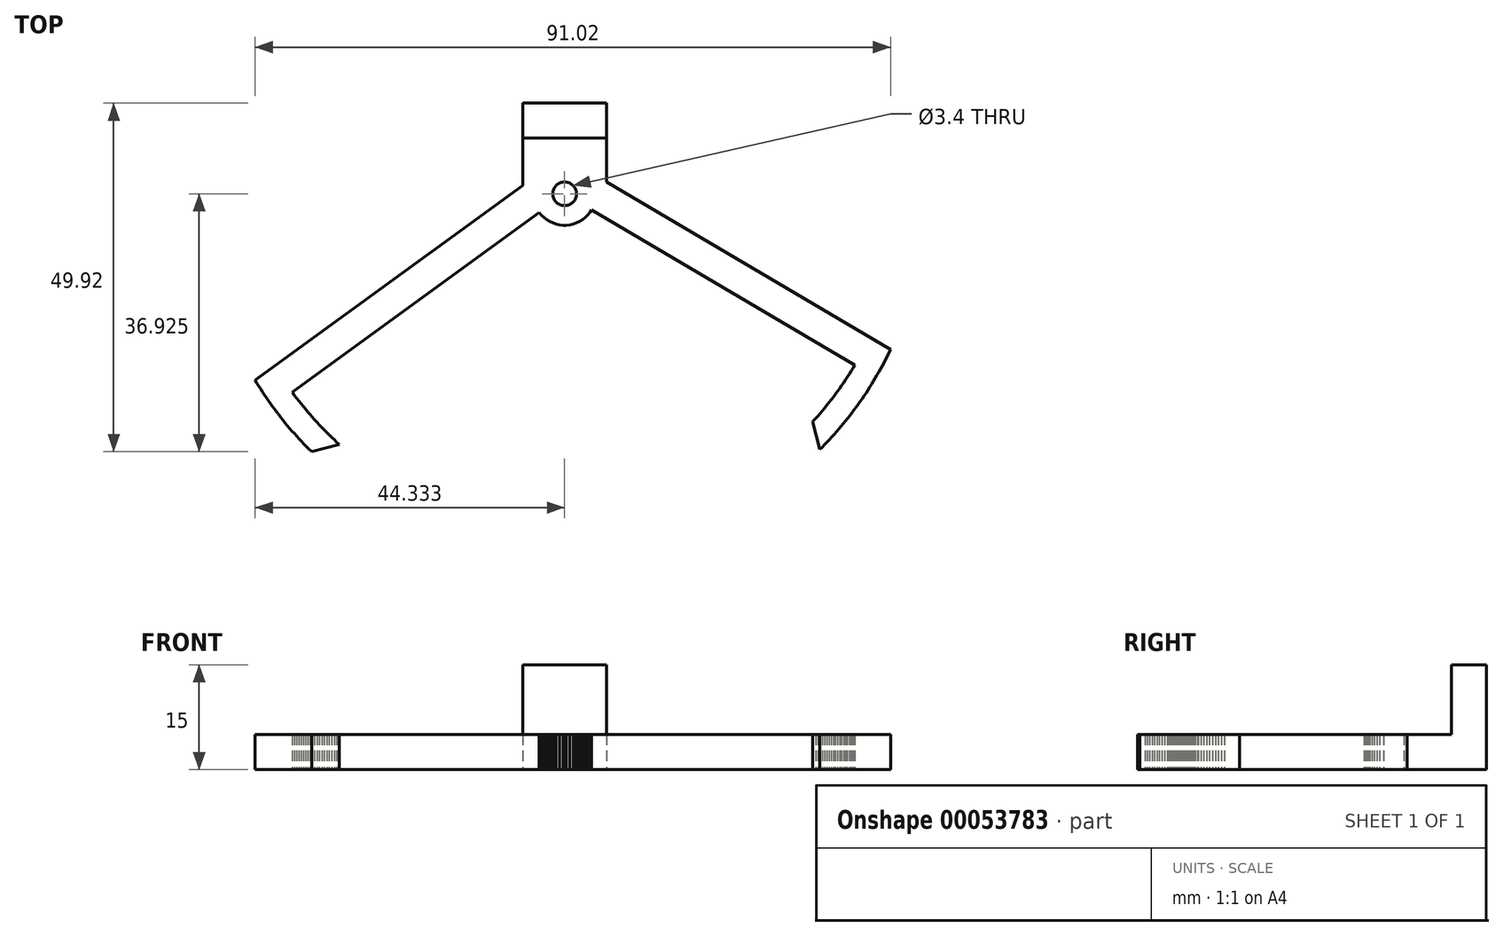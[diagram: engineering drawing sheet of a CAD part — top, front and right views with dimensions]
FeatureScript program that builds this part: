
annotation { "Feature Type Name" : "Feature", "Feature Type Description" : "" }
export const myFeature = defineFeature(function(context is Context, id is Id, definition is map)
    precondition{}
    {
        {
            var Q0;
            Q0=qCreatedBy(makeId("Top.planeOp"),FACE);
            var sketch = newSketch(context, id + "F0", { "sketchPlane" : qUnion([Q0])});
            skLineSegment(sketch, "E0", {"start": v(-33.44, -19.66) * mm, "end": v(-33.81, -19.33) * mm});
            skLineSegment(sketch, "E1", {"start": v(-33.81, -19.33) * mm, "end": v(-34.18, -18.99) * mm});
            skLineSegment(sketch, "E2", {"start": v(-34.18, -18.99) * mm, "end": v(-34.54, -18.64) * mm});
            skLineSegment(sketch, "E3", {"start": v(-34.54, -18.64) * mm, "end": v(-34.9, -18.3) * mm});
            skLineSegment(sketch, "E4", {"start": v(-34.9, -18.3) * mm, "end": v(-35.26, -17.95) * mm});
            skLineSegment(sketch, "E5", {"start": v(-35.26, -17.95) * mm, "end": v(-35.61, -17.6) * mm});
            skLineSegment(sketch, "E6", {"start": v(-35.61, -17.6) * mm, "end": v(-35.96, -17.23) * mm});
            skLineSegment(sketch, "E7", {"start": v(-35.96, -17.23) * mm, "end": v(-36.3, -16.87) * mm});
            skLineSegment(sketch, "E8", {"start": v(-36.3, -16.87) * mm, "end": v(-36.65, -16.5) * mm});
            skLineSegment(sketch, "E9", {"start": v(-36.65, -16.5) * mm, "end": v(-36.98, -16.13) * mm});
            skLineSegment(sketch, "E10", {"start": v(-36.98, -16.13) * mm, "end": v(-37.32, -15.76) * mm});
            skLineSegment(sketch, "E11", {"start": v(-37.32, -15.76) * mm, "end": v(-37.65, -15.39) * mm});
            skLineSegment(sketch, "E12", {"start": v(-37.65, -15.39) * mm, "end": v(-37.97, -15) * mm});
            skLineSegment(sketch, "E13", {"start": v(-37.97, -15) * mm, "end": v(-38.3, -14.62) * mm});
            skLineSegment(sketch, "E14", {"start": v(-38.3, -14.62) * mm, "end": v(-38.6, -14.24) * mm});
            skLineSegment(sketch, "E15", {"start": v(-38.6, -14.24) * mm, "end": v(-38.92, -13.85) * mm});
            skLineSegment(sketch, "E16", {"start": v(-38.92, -13.85) * mm, "end": v(-39.23, -13.45) * mm});
            skLineSegment(sketch, "E17", {"start": v(-39.23, -13.45) * mm, "end": v(-39.54, -13.06) * mm});
            skLineSegment(sketch, "E18", {"start": v(-39.54, -13.06) * mm, "end": v(-39.84, -12.66) * mm});
            skLineSegment(sketch, "E19", {"start": v(-39.84, -12.66) * mm, "end": v(-40.14, -12.26) * mm});
            skLineSegment(sketch, "E20", {"start": v(-40.14, -12.26) * mm, "end": v(-40.2, -12.17) * mm});
            skLineSegment(sketch, "E21", {"start": v(-40.2, -12.17) * mm, "end": v(-4.82, 13.57) * mm});
            skLineSegment(sketch, "E22", {"start": v(-4.82, 13.57) * mm, "end": v(-4.5, 13.18) * mm});
            skLineSegment(sketch, "E23", {"start": v(-4.5, 13.18) * mm, "end": v(-4.14, 12.83) * mm});
            skLineSegment(sketch, "E24", {"start": v(-4.14, 12.83) * mm, "end": v(-3.75, 12.52) * mm});
            skLineSegment(sketch, "E25", {"start": v(-3.75, 12.52) * mm, "end": v(-3.32, 12.26) * mm});
            skLineSegment(sketch, "E26", {"start": v(-3.32, 12.26) * mm, "end": v(-2.87, 12.05) * mm});
            skLineSegment(sketch, "E27", {"start": v(-2.87, 12.05) * mm, "end": v(-2.4, 11.88) * mm});
            skLineSegment(sketch, "E28", {"start": v(-2.4, 11.88) * mm, "end": v(-1.91, 11.78) * mm});
            skLineSegment(sketch, "E29", {"start": v(-1.91, 11.78) * mm, "end": v(-1.42, 11.72) * mm});
            skLineSegment(sketch, "E30", {"start": v(-1.42, 11.72) * mm, "end": v(-0.92, 11.72) * mm});
            skLineSegment(sketch, "E31", {"start": v(-0.92, 11.72) * mm, "end": v(-0.42, 11.78) * mm});
            skLineSegment(sketch, "E32", {"start": v(-0.42, 11.78) * mm, "end": v(0.07, 11.9) * mm});
            skLineSegment(sketch, "E33", {"start": v(0.07, 11.9) * mm, "end": v(0.54, 12.06) * mm});
            skLineSegment(sketch, "E34", {"start": v(0.54, 12.06) * mm, "end": v(1, 12.27) * mm});
            skLineSegment(sketch, "E35", {"start": v(1, 12.27) * mm, "end": v(1.41, 12.54) * mm});
            skLineSegment(sketch, "E36", {"start": v(1.41, 12.54) * mm, "end": v(1.8, 12.85) * mm});
            skLineSegment(sketch, "E37", {"start": v(1.8, 12.85) * mm, "end": v(2.16, 13.2) * mm});
            skLineSegment(sketch, "E38", {"start": v(2.16, 13.2) * mm, "end": v(2.48, 13.59) * mm});
            skLineSegment(sketch, "E39", {"start": v(2.48, 13.59) * mm, "end": v(2.7, 13.93) * mm});
            skLineSegment(sketch, "E40", {"start": v(2.7, 13.93) * mm, "end": v(40.39, -8.3) * mm});
            skLineSegment(sketch, "E41", {"start": v(40.39, -8.3) * mm, "end": v(40.13, -8.73) * mm});
            skLineSegment(sketch, "E42", {"start": v(40.13, -8.73) * mm, "end": v(39.87, -9.16) * mm});
            skLineSegment(sketch, "E43", {"start": v(39.87, -9.16) * mm, "end": v(39.6, -9.58) * mm});
            skLineSegment(sketch, "E44", {"start": v(39.6, -9.58) * mm, "end": v(39.34, -10) * mm});
            skLineSegment(sketch, "E45", {"start": v(39.34, -10) * mm, "end": v(39.06, -10.42) * mm});
            skLineSegment(sketch, "E46", {"start": v(39.06, -10.42) * mm, "end": v(38.78, -10.84) * mm});
            skLineSegment(sketch, "E47", {"start": v(38.78, -10.84) * mm, "end": v(38.5, -11.25) * mm});
            skLineSegment(sketch, "E48", {"start": v(38.5, -11.25) * mm, "end": v(38.21, -11.66) * mm});
            skLineSegment(sketch, "E49", {"start": v(38.21, -11.66) * mm, "end": v(37.92, -12.06) * mm});
            skLineSegment(sketch, "E50", {"start": v(37.92, -12.06) * mm, "end": v(37.63, -12.47) * mm});
            skLineSegment(sketch, "E51", {"start": v(37.63, -12.47) * mm, "end": v(37.33, -12.87) * mm});
            skLineSegment(sketch, "E52", {"start": v(37.33, -12.87) * mm, "end": v(37.03, -13.27) * mm});
            skLineSegment(sketch, "E53", {"start": v(37.03, -13.27) * mm, "end": v(36.72, -13.66) * mm});
            skLineSegment(sketch, "E54", {"start": v(36.72, -13.66) * mm, "end": v(36.4, -14.05) * mm});
            skLineSegment(sketch, "E55", {"start": v(36.4, -14.05) * mm, "end": v(36.1, -14.44) * mm});
            skLineSegment(sketch, "E56", {"start": v(36.1, -14.44) * mm, "end": v(35.77, -14.82) * mm});
            skLineSegment(sketch, "E57", {"start": v(35.77, -14.82) * mm, "end": v(35.45, -15.2) * mm});
            skLineSegment(sketch, "E58", {"start": v(35.45, -15.2) * mm, "end": v(35.12, -15.58) * mm});
            skLineSegment(sketch, "E59", {"start": v(35.12, -15.58) * mm, "end": v(34.79, -15.96) * mm});
            skLineSegment(sketch, "E60", {"start": v(34.79, -15.96) * mm, "end": v(34.45, -16.33) * mm});
            skLineSegment(sketch, "E61", {"start": v(34.45, -16.33) * mm, "end": v(34.38, -16.4) * mm});
            skLineSegment(sketch, "E62", {"start": v(34.38, -16.4) * mm, "end": v(35.4, -20.4) * mm});
            skLineSegment(sketch, "E63", {"start": v(35.4, -20.4) * mm, "end": v(35.74, -20.04) * mm});
            skLineSegment(sketch, "E64", {"start": v(35.74, -20.04) * mm, "end": v(36.1, -19.68) * mm});
            skLineSegment(sketch, "E65", {"start": v(36.1, -19.68) * mm, "end": v(36.44, -19.32) * mm});
            skLineSegment(sketch, "E66", {"start": v(36.44, -19.32) * mm, "end": v(36.78, -18.96) * mm});
            skLineSegment(sketch, "E67", {"start": v(36.78, -18.96) * mm, "end": v(37.12, -18.59) * mm});
            skLineSegment(sketch, "E68", {"start": v(37.12, -18.59) * mm, "end": v(37.45, -18.22) * mm});
            skLineSegment(sketch, "E69", {"start": v(37.45, -18.22) * mm, "end": v(37.78, -17.84) * mm});
            skLineSegment(sketch, "E70", {"start": v(37.78, -17.84) * mm, "end": v(38.1, -17.46) * mm});
            skLineSegment(sketch, "E71", {"start": v(38.1, -17.46) * mm, "end": v(38.43, -17.08) * mm});
            skLineSegment(sketch, "E72", {"start": v(38.43, -17.08) * mm, "end": v(38.75, -16.7) * mm});
            skLineSegment(sketch, "E73", {"start": v(38.75, -16.7) * mm, "end": v(39.07, -16.3) * mm});
            skLineSegment(sketch, "E74", {"start": v(39.07, -16.3) * mm, "end": v(39.38, -15.92) * mm});
            skLineSegment(sketch, "E75", {"start": v(39.38, -15.92) * mm, "end": v(39.69, -15.53) * mm});
            skLineSegment(sketch, "E76", {"start": v(39.69, -15.53) * mm, "end": v(40, -15.13) * mm});
            skLineSegment(sketch, "E77", {"start": v(40, -15.13) * mm, "end": v(40.3, -14.73) * mm});
            skLineSegment(sketch, "E78", {"start": v(40.3, -14.73) * mm, "end": v(40.6, -14.33) * mm});
            skLineSegment(sketch, "E79", {"start": v(40.6, -14.33) * mm, "end": v(40.89, -13.92) * mm});
            skLineSegment(sketch, "E80", {"start": v(40.89, -13.92) * mm, "end": v(41.17, -13.52) * mm});
            skLineSegment(sketch, "E81", {"start": v(41.17, -13.52) * mm, "end": v(41.46, -13.1) * mm});
            skLineSegment(sketch, "E82", {"start": v(41.46, -13.1) * mm, "end": v(41.74, -12.7) * mm});
            skLineSegment(sketch, "E83", {"start": v(41.74, -12.7) * mm, "end": v(42.02, -12.28) * mm});
            skLineSegment(sketch, "E84", {"start": v(42.02, -12.28) * mm, "end": v(42.3, -11.86) * mm});
            skLineSegment(sketch, "E85", {"start": v(42.3, -11.86) * mm, "end": v(42.56, -11.44) * mm});
            skLineSegment(sketch, "E86", {"start": v(42.56, -11.44) * mm, "end": v(42.83, -11.01) * mm});
            skLineSegment(sketch, "E87", {"start": v(42.83, -11.01) * mm, "end": v(43.09, -10.58) * mm});
            skLineSegment(sketch, "E88", {"start": v(43.09, -10.58) * mm, "end": v(43.34, -10.16) * mm});
            skLineSegment(sketch, "E89", {"start": v(43.34, -10.16) * mm, "end": v(43.6, -9.72) * mm});
            skLineSegment(sketch, "E90", {"start": v(43.6, -9.72) * mm, "end": v(43.85, -9.3) * mm});
            skLineSegment(sketch, "E91", {"start": v(43.85, -9.3) * mm, "end": v(44.09, -8.85) * mm});
            skLineSegment(sketch, "E92", {"start": v(44.09, -8.85) * mm, "end": v(44.33, -8.42) * mm});
            skLineSegment(sketch, "E93", {"start": v(44.33, -8.42) * mm, "end": v(44.57, -7.98) * mm});
            skLineSegment(sketch, "E94", {"start": v(44.57, -7.98) * mm, "end": v(44.8, -7.53) * mm});
            skLineSegment(sketch, "E95", {"start": v(44.8, -7.53) * mm, "end": v(45.02, -7.09) * mm});
            skLineSegment(sketch, "E96", {"start": v(45.02, -7.09) * mm, "end": v(45.25, -6.64) * mm});
            skLineSegment(sketch, "E97", {"start": v(45.25, -6.64) * mm, "end": v(45.47, -6.19) * mm});
            skLineSegment(sketch, "E98", {"start": v(45.47, -6.19) * mm, "end": v(45.51, -6.1) * mm});
            skLineSegment(sketch, "E99", {"start": v(45.51, -6.1) * mm, "end": v(1.1, 20.1) * mm});
            skLineSegment(sketch, "E100", {"start": v(1.1, 20.1) * mm, "end": v(0.67, 20.32) * mm});
            skLineSegment(sketch, "E101", {"start": v(0.67, 20.32) * mm, "end": v(0.2, 20.5) * mm});
            skLineSegment(sketch, "E102", {"start": v(0.2, 20.5) * mm, "end": v(-0.28, 20.63) * mm});
            skLineSegment(sketch, "E103", {"start": v(-0.28, 20.63) * mm, "end": v(-0.78, 20.7) * mm});
            skLineSegment(sketch, "E104", {"start": v(-0.78, 20.7) * mm, "end": v(-1.28, 20.71) * mm});
            skLineSegment(sketch, "E105", {"start": v(-1.28, 20.71) * mm, "end": v(-1.78, 20.67) * mm});
            skLineSegment(sketch, "E106", {"start": v(-1.78, 20.67) * mm, "end": v(-2.27, 20.58) * mm});
            skLineSegment(sketch, "E107", {"start": v(-2.27, 20.58) * mm, "end": v(-2.75, 20.43) * mm});
            skLineSegment(sketch, "E108", {"start": v(-2.75, 20.43) * mm, "end": v(-3.2, 20.23) * mm});
            skLineSegment(sketch, "E109", {"start": v(-3.2, 20.23) * mm, "end": v(-3.64, 19.98) * mm});
            skLineSegment(sketch, "E110", {"start": v(-3.64, 19.98) * mm, "end": v(-3.82, 19.85) * mm});
            skLineSegment(sketch, "E111", {"start": v(-3.82, 19.85) * mm, "end": v(-45.51, -10.47) * mm});
            skLineSegment(sketch, "E112", {"start": v(-45.51, -10.47) * mm, "end": v(-45.25, -10.9) * mm});
            skLineSegment(sketch, "E113", {"start": v(-45.25, -10.9) * mm, "end": v(-44.99, -11.32) * mm});
            skLineSegment(sketch, "E114", {"start": v(-44.99, -11.32) * mm, "end": v(-44.72, -11.74) * mm});
            skLineSegment(sketch, "E115", {"start": v(-44.72, -11.74) * mm, "end": v(-44.45, -12.16) * mm});
            skLineSegment(sketch, "E116", {"start": v(-44.45, -12.16) * mm, "end": v(-44.17, -12.58) * mm});
            skLineSegment(sketch, "E117", {"start": v(-44.17, -12.58) * mm, "end": v(-43.89, -13) * mm});
            skLineSegment(sketch, "E118", {"start": v(-43.89, -13) * mm, "end": v(-43.6, -13.4) * mm});
            skLineSegment(sketch, "E119", {"start": v(-43.6, -13.4) * mm, "end": v(-43.32, -13.81) * mm});
            skLineSegment(sketch, "E120", {"start": v(-43.32, -13.81) * mm, "end": v(-43.02, -14.22) * mm});
            skLineSegment(sketch, "E121", {"start": v(-43.02, -14.22) * mm, "end": v(-42.73, -14.62) * mm});
            skLineSegment(sketch, "E122", {"start": v(-42.73, -14.62) * mm, "end": v(-42.43, -15.02) * mm});
            skLineSegment(sketch, "E123", {"start": v(-42.43, -15.02) * mm, "end": v(-42.13, -15.42) * mm});
            skLineSegment(sketch, "E124", {"start": v(-42.13, -15.42) * mm, "end": v(-41.82, -15.81) * mm});
            skLineSegment(sketch, "E125", {"start": v(-41.82, -15.81) * mm, "end": v(-41.5, -16.2) * mm});
            skLineSegment(sketch, "E126", {"start": v(-41.5, -16.2) * mm, "end": v(-41.2, -16.6) * mm});
            skLineSegment(sketch, "E127", {"start": v(-41.2, -16.6) * mm, "end": v(-40.87, -16.98) * mm});
            skLineSegment(sketch, "E128", {"start": v(-40.87, -16.98) * mm, "end": v(-40.55, -17.36) * mm});
            skLineSegment(sketch, "E129", {"start": v(-40.55, -17.36) * mm, "end": v(-40.22, -17.74) * mm});
            skLineSegment(sketch, "E130", {"start": v(-40.22, -17.74) * mm, "end": v(-39.9, -18.12) * mm});
            skLineSegment(sketch, "E131", {"start": v(-39.9, -18.12) * mm, "end": v(-39.56, -18.49) * mm});
            skLineSegment(sketch, "E132", {"start": v(-39.56, -18.49) * mm, "end": v(-39.22, -18.86) * mm});
            skLineSegment(sketch, "E133", {"start": v(-39.22, -18.86) * mm, "end": v(-38.88, -19.22) * mm});
            skLineSegment(sketch, "E134", {"start": v(-38.88, -19.22) * mm, "end": v(-38.54, -19.59) * mm});
            skLineSegment(sketch, "E135", {"start": v(-38.54, -19.59) * mm, "end": v(-38.2, -19.95) * mm});
            skLineSegment(sketch, "E136", {"start": v(-38.2, -19.95) * mm, "end": v(-37.84, -20.3) * mm});
            skLineSegment(sketch, "E137", {"start": v(-37.84, -20.3) * mm, "end": v(-37.48, -20.65) * mm});
            skLineSegment(sketch, "E138", {"start": v(-37.48, -20.65) * mm, "end": v(-37.42, -20.71) * mm});
            skLineSegment(sketch, "E139", {"start": v(-37.42, -20.71) * mm, "end": v(-33.44, -19.66) * mm});
            skCircle(sketch, "E140", {"center": v(-1.18, 16.21) * mm, "radius": 1.7 * mm});
            skPoint(sketch, "E141", {"position": v(-7.24, 17.37) * mm});
            skLineSegment(sketch, "E142", {"start": v(-2.68, 29.21) * mm, "end": v(-2.68, 24.21) * mm});
            skLineSegment(sketch, "E143", {"start": v(0.32, 29.21) * mm, "end": v(0.32, 24.21) * mm});
            skLineSegment(sketch, "E144", {"start": v(-7.18, 29.21) * mm, "end": v(4.82, 29.21) * mm});
            skLineSegment(sketch, "E145", {"start": v(-7.18, 24.21) * mm, "end": v(4.82, 24.21) * mm});
            skLineSegment(sketch, "E146", {"start": v(4.82, 13.73) * mm, "end": v(4.82, 29.21) * mm});
            skLineSegment(sketch, "E147", {"start": v(-1.18, 29.21) * mm, "end": v(-1.18, 13.73) * mm, "construction": true});
            skLineSegment(sketch, "E148", {"start": v(-7.18, 13.73) * mm, "end": v(-7.18, 29.21) * mm});
            skCircle(sketch, "E149", {"center": v(-1.18, 16.21) * mm, "radius": 4 * mm});
            skLineSegment(sketch, "E150", {"start": v(-7.18, 16.21) * mm, "end": v(4.82, 16.21) * mm, "construction": true});
            skLineSegment(sketch, "E151", {"start": v(-7.18, 13.73) * mm, "end": v(4.82, 13.73) * mm});
            skSolve(sketch);
        }
        {
            var Q0;
            Q0=makeQuery(id+"F0.imprint","IMPRINT",FACE,{"disambiguationData":[TD([[makeQuery(id+"F0.imprint","IMPRINT",EDGE,{"derivedFrom":sQuery(id+"F0.wireOp",EDGE,"E0")}),1.0]])]});
            var Q1;
            {var subQ5=sQuery(id+"F0.wireOp",EDGE,"E40");Q1=makeQuery(id+"F0.imprint","IMPRINT",FACE,{"disambiguationData":[TD([[makeQuery(id+"F0.imprint","IMPRINT",EDGE,{"derivedFrom":subQ5}),1.0]])]});}
            var Q2;
            {var subQ4=sQuery(id+"F0.wireOp",EDGE,"E22");Q2=makeQuery(id+"F0.imprint","IMPRINT",FACE,{"disambiguationData":[TD([[makeQuery(id+"F0.imprint","IMPRINT",EDGE,{"derivedFrom":subQ4}),1.0]])]});}
            var Q3;
            {var subQ0=sQuery(id+"F0.wireOp",EDGE,"7Wl6hOCf-y8FN-YXAg-lJnB-ywVYcL8Pvd7c");Q3=makeQuery(id+"F0.imprint","IMPRINT",FACE,{"disambiguationData":[TD([[makeQuery(id+"F0.imprint","IMPRINT",EDGE,{"derivedFrom":subQ0}),1.0]])]});}
            var Q4;
            {var subQ7=sQuery(id+"F0.wireOp",EDGE,"E100");Q4=makeQuery(id+"F0.imprint","IMPRINT",FACE,{"disambiguationData":[TD([[makeQuery(id+"F0.imprint","IMPRINT",EDGE,{"derivedFrom":subQ7}),-1.0]])]});}
            var Q5;
            {var subQ0=sQuery(id+"F0.wireOp",EDGE,"E100");Q5=makeQuery(id+"F0.imprint","IMPRINT",FACE,{"disambiguationData":[TD([[makeQuery(id+"F0.imprint","IMPRINT",EDGE,{"derivedFrom":subQ0}),1.0]])]});}
            var Q6;
            Q6=makeQuery(id+"F0.imprint","IMPRINT",FACE,{"disambiguationData":[TD([[makeQuery(id+"F0.imprint","IMPRINT",EDGE,{"derivedFrom":sQuery(id+"F0.wireOp",EDGE,"E0")}),1.0]])]});
            var Q7;
            Q7=makeQuery(id+"F0.imprint","IMPRINT",FACE,{"disambiguationData":[TD([[makeQuery(id+"F0.imprint","IMPRINT",EDGE,{"derivedFrom":sQuery(id+"F0.wireOp",EDGE,"E140")}),-1.0]])]});
            var Q8;
            {var subQ0=sQuery(id+"F0.wireOp",EDGE,"gpeoCXvY-1RkU-sdRD-Jcin-rU8xiW87tctx");var subQ1=sQuery(id+"F0.wireOp",EDGE,"ac43ed41-176c-43a0-8963-aafd62ddca72");var subQ2=makeQuery(id+"F0.imprint","INTERSECT",VERTEX,{"disambiguationData":[OD(0.0)],"derivedFrom":[subQ1,subQ0]});Q8=makeQuery(id+"F0.imprint","IMPRINT",FACE,{"disambiguationData":[TD([[makeQuery(id+"F0.imprint","IMPRINT",EDGE,{"disambiguationData":[TD([[subQ2,-1.0]])],"derivedFrom":subQ1}),1.0]])]});}
            var Q9;
            {var subQ0=sQuery(id+"F0.wireOp",EDGE,"E41");Q9=makeQuery(id+"F0.imprint","IMPRINT",FACE,{"disambiguationData":[TD([[makeQuery(id+"F0.imprint","IMPRINT",EDGE,{"derivedFrom":subQ0}),1.0]])]});}
            var Q10;
            {var subQ0=sQuery(id+"F0.wireOp",EDGE,"E151");var subQ1=sQuery(id+"F0.wireOp",EDGE,"E149");var subQ2=makeQuery(id+"F0.imprint","INTERSECT",VERTEX,{"disambiguationData":[OD(0.0)],"derivedFrom":[subQ1,subQ0]});Q10=makeQuery(id+"F0.imprint","IMPRINT",FACE,{"disambiguationData":[TD([[makeQuery(id+"F0.imprint","IMPRINT",EDGE,{"disambiguationData":[TD([[subQ2,-1.0]])],"derivedFrom":subQ1}),1.0]])]});}
            var Q11;
            Q11=makeQuery(id+"F0.imprint","IMPRINT",FACE,{"disambiguationData":[TD([[makeQuery(id+"F0.imprint","IMPRINT",EDGE,{"derivedFrom":sQuery(id+"F0.wireOp",EDGE,"a5ee5e0a-0ed0-45e9-a193-4ad686f830aa")}),-1.0]])]});
            extrude(context, id + "F1", {"entities" : qUnion([Q0, Q1, Q2, Q3, Q4, Q5, Q6, Q7, Q8, Q9, Q10, Q11]), "depth" : 5 * mm});
        }
        {
            var Q0;
            {var subQ0=sQuery(id+"F0.wireOp",EDGE,"E142");Q0=makeQuery(id+"F0.imprint","IMPRINT",FACE,{"disambiguationData":[TD([[makeQuery(id+"F0.imprint","IMPRINT",EDGE,{"derivedFrom":subQ0}),-1.0]])]});}
            var Q1;
            {var subQ0=sQuery(id+"F0.wireOp",EDGE,"E143");Q1=makeQuery(id+"F0.imprint","IMPRINT",FACE,{"disambiguationData":[TD([[makeQuery(id+"F0.imprint","IMPRINT",EDGE,{"derivedFrom":subQ0}),1.0]])]});}
            var Q2;
            {var subQ0=sQuery(id+"F0.wireOp",EDGE,"E142");Q2=makeQuery(id+"F0.imprint","IMPRINT",FACE,{"disambiguationData":[TD([[makeQuery(id+"F0.imprint","IMPRINT",EDGE,{"derivedFrom":subQ0}),1.0]])]});}
            extrude(context, id + "F2", {"entities" : qUnion([Q0, Q1, Q2]), "operationType" : NewBodyOperationType.ADD, "depth" : 15 * mm});
        }
    });
